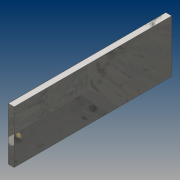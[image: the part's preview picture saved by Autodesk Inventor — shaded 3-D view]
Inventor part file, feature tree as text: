
AUTODESK INVENTOR PART (.ipt)
format: ipt  version: 2021 (Build 250183000, 183)  size: 95,744 bytes
history: native  units: mm
features: extrude x1, sketch x1
ambient origin geometry x8: Origin, YZ Plane, XZ Plane, XY Plane, X Axis, Y Axis, Z Axis, Center Point
bodies: Solid1 (feature_tree)
feature tree (2):
  extrude  "Extrusion1"  Depth=270.0mm
  sketch  "Sketch1"  dims[d0=90.0mm d1=270.0mm d2=10.0mm d3=0.0mm]
